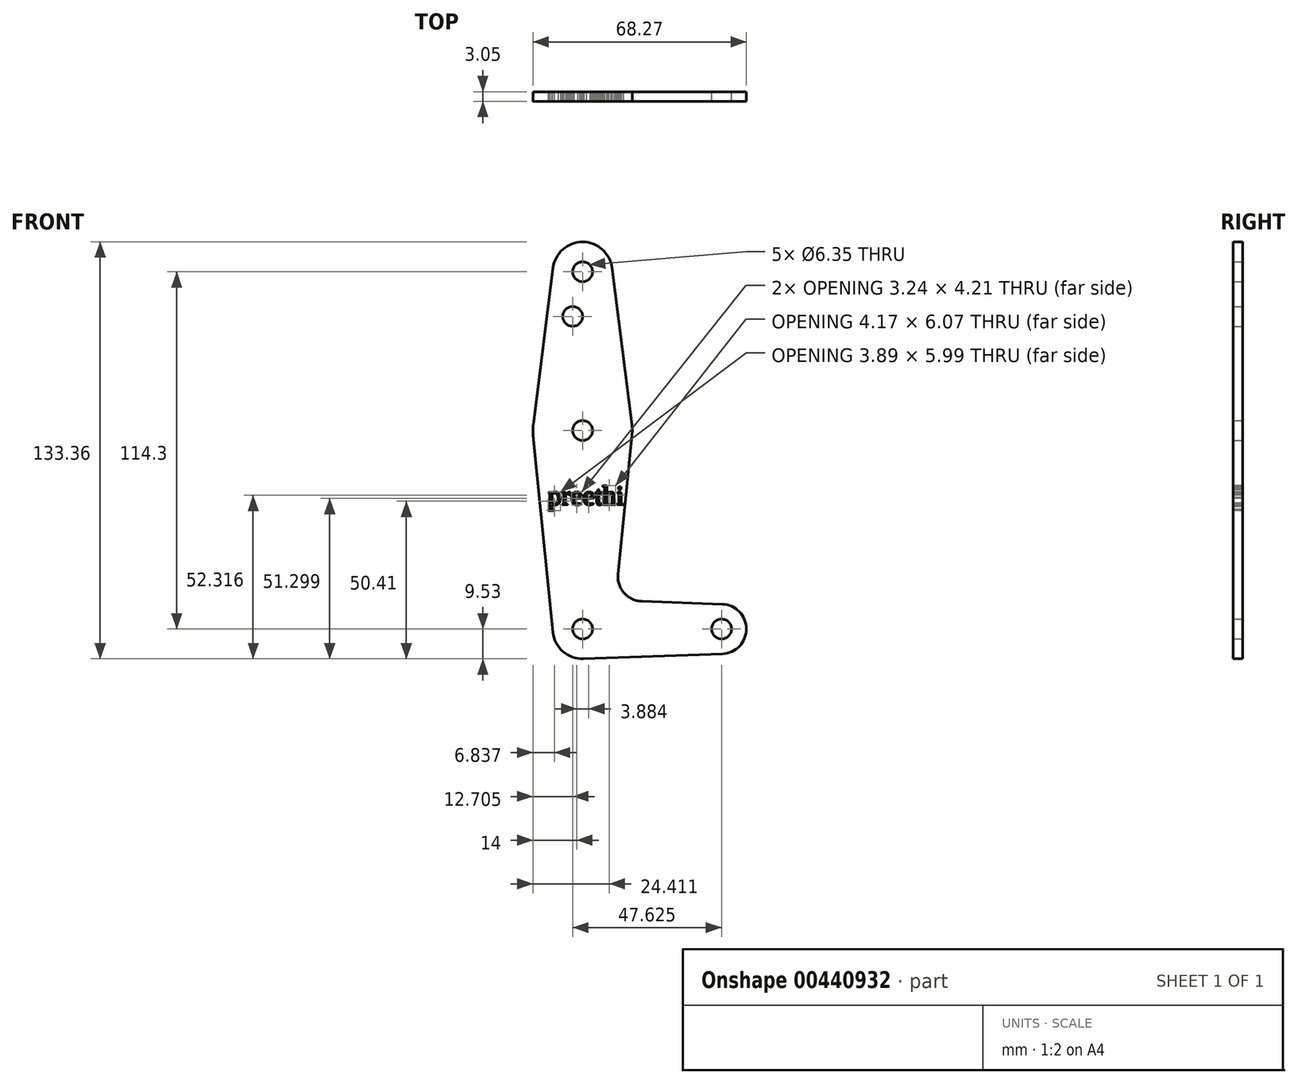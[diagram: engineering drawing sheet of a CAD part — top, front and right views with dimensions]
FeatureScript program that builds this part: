
annotation { "Feature Type Name" : "Feature", "Feature Type Description" : "" }
export const myFeature = defineFeature(function(context is Context, id is Id, definition is map)
    precondition{}
    {
        {
            var Q0;
            Q0=qCreatedBy(makeId("Front.planeOp"),FACE);
            var sketch = newSketch(context, id + "F0", { "sketchPlane" : qUnion([Q0])});
            skLineSegment(sketch, "E0", {"start": v(0, 0) * mm, "end": v(0, 114.3) * mm});
            skLineSegment(sketch, "E1", {"start": v(0, 0) * mm, "end": v(44.45, 0) * mm});
            skCircle(sketch, "E2", {"center": v(0, 114.3) * mm, "radius": 9.53 * mm});
            skCircle(sketch, "E3", {"center": v(0, 63.5) * mm, "radius": 15.88 * mm});
            skCircle(sketch, "E4", {"center": v(0, 0) * mm, "radius": 9.53 * mm});
            skCircle(sketch, "E5", {"center": v(44.45, 0) * mm, "radius": 7.94 * mm});
            skLineSegment(sketch, "E6", {"start": v(-9.45, 115.5) * mm, "end": v(-15.75, 65.48) * mm});
            skLineSegment(sketch, "E7", {"start": v(9.45, 115.5) * mm, "end": v(15.75, 65.48) * mm});
            skLineSegment(sketch, "E8", {"start": v(-15.8, 61.91) * mm, "end": v(-9.48, -0.95) * mm});
            skLineSegment(sketch, "E9", {"start": v(15.8, 61.91) * mm, "end": v(11.34, 17.6) * mm});
            skLineSegment(sketch, "E10", {"start": v(18.97, 8.85) * mm, "end": v(44.73, 7.93) * mm});
            skLineSegment(sketch, "E11", {"start": v(0.34, -9.52) * mm, "end": v(44.73, -7.93) * mm});
            skCircle(sketch, "E12", {"center": v(0, 114.3) * mm, "radius": 3.18 * mm});
            skCircle(sketch, "E13", {"center": v(-3.18, 100.03) * mm, "radius": 3.18 * mm});
            skCircle(sketch, "E14", {"center": v(0, 63.5) * mm, "radius": 3.18 * mm});
            skCircle(sketch, "E15", {"center": v(44.45, 0) * mm, "radius": 3.18 * mm});
            skArc(sketch, "E16.filletArc", {"start": v(11.34, 17.6) * mm, "mid": v(13.26, 11.57) * mm, "end": v(18.97, 8.85) * mm});
            skCircle(sketch, "E17", {"center": v(0, 0) * mm, "radius": 3.18 * mm});
            skSolve(sketch);
        }
        {
            var Q0;
            Q0 = qSketchRegion(id + "F0", true);
            var Q1;
            {var subQ0=sQuery(id+"F0.wireOp",EDGE,"E17");var subQ1=sQuery(id+"F0.wireOp",EDGE,"E0");var subQ2=makeQuery(id+"F0.imprint","INTERSECT",VERTEX,{"derivedFrom":[subQ1,subQ0]});Q1=makeQuery(id+"F0.imprint","IMPRINT",FACE,{"disambiguationData":[TD([[makeQuery(id+"F0.imprint","IMPRINT",EDGE,{"disambiguationData":[TD([[subQ2,-1.0]])],"derivedFrom":subQ1}),-1.0]])]});}
            extrude(context, id + "F1", {"entities" : qUnion([Q0, Q1]), "depth" : 3.05 * mm});
        }
        {
            var Q0;
            Q0=makeQuery(id+"F1.opExtrude","CAP_FACE",FACE,{"disambiguationData":[OSD([sQuery(id+"F0.wireOp",EDGE,"E2"),sQuery(id+"F0.wireOp",EDGE,"E3"),sQuery(id+"F0.wireOp",EDGE,"E4"),sQuery(id+"F0.wireOp",EDGE,"E5"),sQuery(id+"F0.wireOp",EDGE,"E6"),sQuery(id+"F0.wireOp",EDGE,"E7"),sQuery(id+"F0.wireOp",EDGE,"E8"),sQuery(id+"F0.wireOp",EDGE,"E9"),sQuery(id+"F0.wireOp",EDGE,"E10"),sQuery(id+"F0.wireOp",EDGE,"E11"),sQuery(id+"F0.wireOp",EDGE,"E12"),sQuery(id+"F0.wireOp",EDGE,"E13"),sQuery(id+"F0.wireOp",EDGE,"E14"),sQuery(id+"F0.wireOp",EDGE,"E15"),sQuery(id+"F0.wireOp",EDGE,"E16.filletArc"),sQuery(id+"F0.wireOp",EDGE,"E17")])],"isStart":false});
            var sketch = newSketch(context, id + "F2", { "sketchPlane" : qUnion([Q0])});
            skText(sketch, "E18", { "text": "preethi", "fontName": "Tinos-Regular.ttf"});
            const initialGuessF2  = {"E18": [-0.01113, 0.03975, 1, 0, 0.0063]};
            skSetInitialGuess(sketch, initialGuessF2);
            skSolve(sketch);
        }
        {
            var Q0;
            Q0 = qSketchRegion(id + "F2", true);
            extrude(context, id + "F3", {"entities" : qUnion([Q0]), "operationType" : NewBodyOperationType.REMOVE, "oppositeDirection" : true, "depth" : 25.4 * mm});
        }
    });
